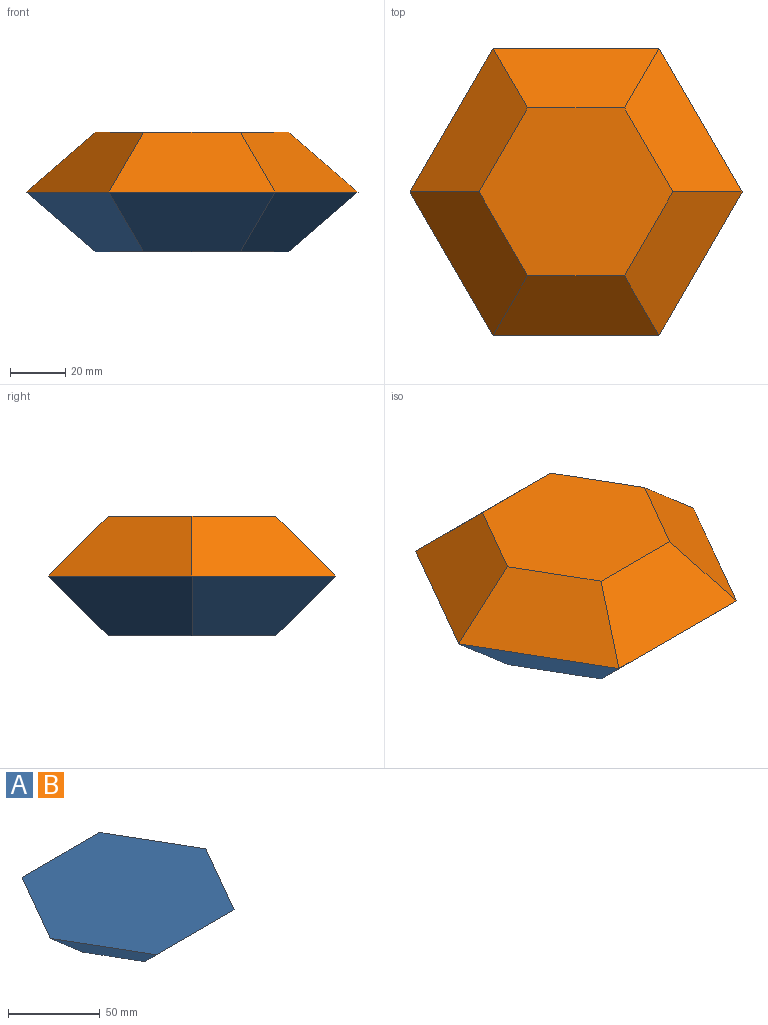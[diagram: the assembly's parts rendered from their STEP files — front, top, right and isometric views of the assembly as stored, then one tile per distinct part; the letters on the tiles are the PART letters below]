
ASSEMBLY  parts=2 mates=1
PART A: 8 faces, bbox 119.8x103.7x21.6 mm
  f0: plane 51.86x42.41mm, normal (0.61,-0.35,-0.71), area 1447.9mm2, adj f1,f5,f6,f7
  f1: plane 51.86x42.41mm, normal (0.61,0.35,-0.71), area 1447.9mm2, adj f0,f2,f6,f7
  f2: plane 59.89x21.59mm, normal (0,0.71,-0.71), area 1447.9mm2, adj f1,f3,f6,f7
  f3: plane 51.86x42.41mm, normal (-0.61,0.35,-0.71), area 1447.9mm2, adj f2,f4,f6,f7
  f4: plane 51.86x42.41mm, normal (-0.61,-0.35,-0.71), area 1447.9mm2, adj f3,f5,f6,f7
  f5: plane 59.89x21.59mm, normal (0,-0.71,-0.71), area 1447.9mm2, adj f0,f4,f6,f7
  f6: plane 119.77x103.73mm, normal (0,0,1), area 9317.5mm2, adj f0,f1,f2,f3,f4,f5
  f7: plane 69.91x60.55mm, normal (0,0,-1), area 3174.6mm2, adj f0,f1,f2,f3,f4,f5
PART B: same geometry as A
PLACE A t=(52.52,31.18,-10.8)mm
PLACE B rot(axis=(1,0,0),180deg) t=(52.52,31.18,32.38)mm
MATE fastened B.f6 <-> A.f6  axis (0,0,-1) through (52.52,31.18,10.79)mm
